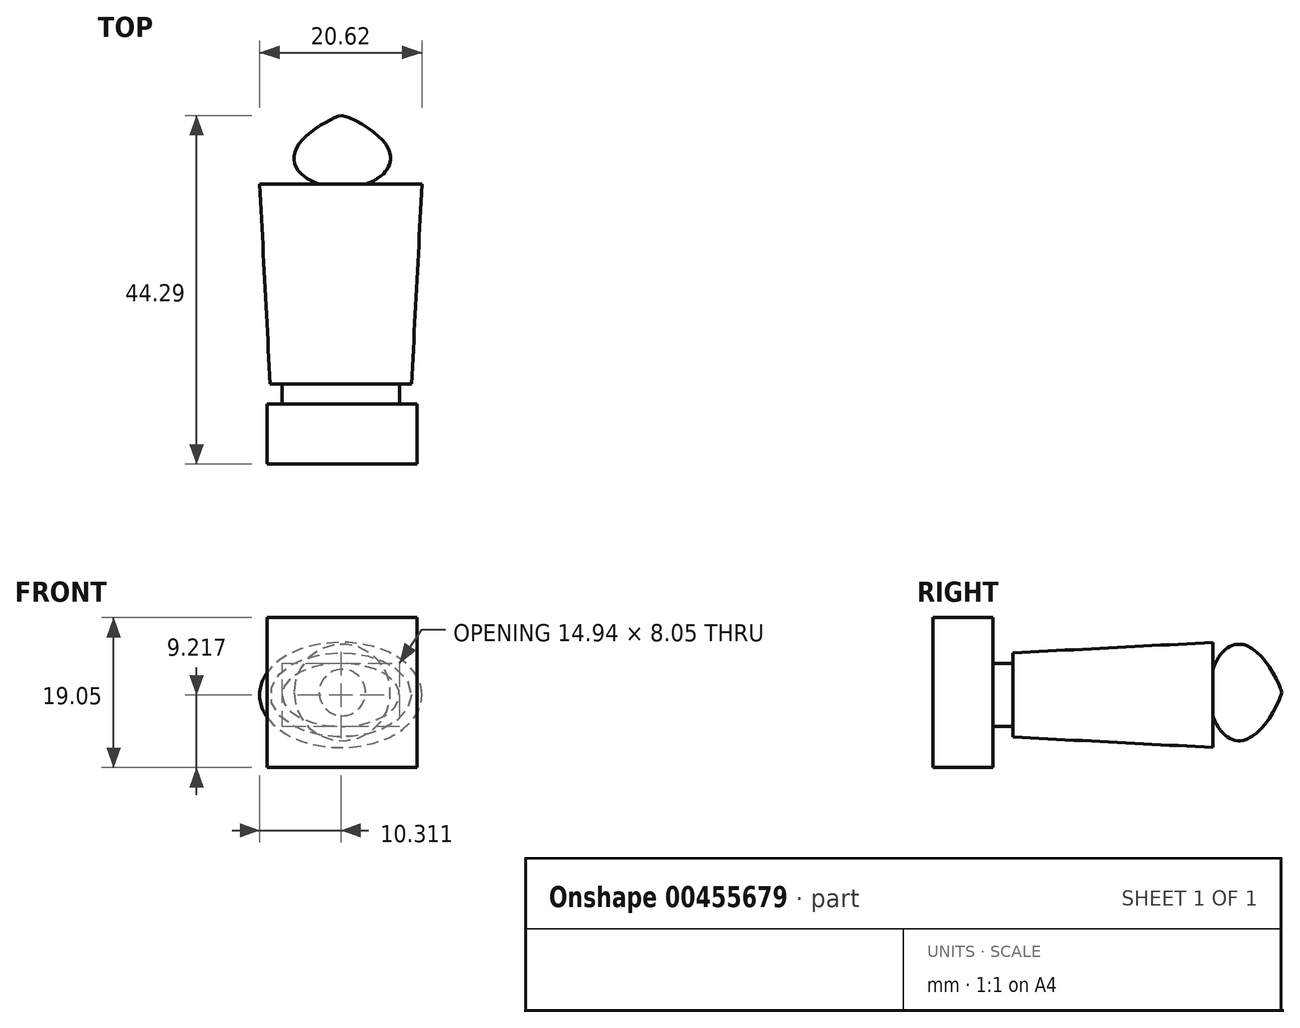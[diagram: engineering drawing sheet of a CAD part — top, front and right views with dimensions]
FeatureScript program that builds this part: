
annotation { "Feature Type Name" : "Feature", "Feature Type Description" : "" }
export const myFeature = defineFeature(function(context is Context, id is Id, definition is map)
    precondition{}
    {
        {
            var Q0;
            Q0=qCreatedBy(makeId("Front.planeOp"),FACE);
            var sketch = newSketch(context, id + "F0", { "sketchPlane" : qUnion([Q0])});
            skLineSegment(sketch, "E0.bottom", {"start": v(0, 0) * mm, "end": v(-19.05, 0) * mm});
            skLineSegment(sketch, "E0.top", {"start": v(0, 19.05) * mm, "end": v(-19.05, 19.05) * mm});
            skLineSegment(sketch, "E0.left", {"start": v(0, 0) * mm, "end": v(0, 19.05) * mm});
            skLineSegment(sketch, "E0.right", {"start": v(-19.05, 0) * mm, "end": v(-19.05, 19.05) * mm});
            skPoint(sketch, "E1", {"position": v(-9.53, 9.52) * mm});
            skPoint(sketch, "E1.positionSnap0", {"position": v(-19.05, 9.52) * mm});
            skPoint(sketch, "E1.positionSnap1", {"position": v(-9.53, 19.05) * mm});
            skSolve(sketch);
        }
        {
            var Q0;
            Q0=makeQuery(id+"F0.imprint","IMPRINT",FACE,{"disambiguationData":[TD([[makeQuery(id+"F0.imprint","IMPRINT",EDGE,{"derivedFrom":sQuery(id+"F0.wireOp",EDGE,"E0.bottom")}),-1.0]])]});
            extrude(context, id + "F1", {"entities" : qUnion([Q0]), "depth" : 7.62 * mm});
        }
        {
            var Q0;
            Q0=qCreatedBy(makeId("Front.planeOp"),FACE);
            var sketch = newSketch(context, id + "F2", { "sketchPlane" : qUnion([Q0])});
            skPoint(sketch, "E2", {"position": v(-9.7, 9.22) * mm});
            skEllipse(sketch, "E3", {"center": v(-9.7, 9.22) * mm, "majorRadius": 7.47 * mm, "minorRadius": 4.02 * mm, "majorAxis": v(-1, 0)});
            skSolve(sketch);
        }
        {
            var Q0;
            Q0=makeQuery(id+"F2.imprint","IMPRINT",FACE,{"disambiguationData":[TD([[makeQuery(id+"F2.imprint","IMPRINT",EDGE,{"derivedFrom":sQuery(id+"F2.wireOp",EDGE,"E3")}),1.0]])]});
            extrude(context, id + "F3", {"entities" : qUnion([Q0]), "operationType" : NewBodyOperationType.ADD, "oppositeDirection" : true, "depth" : 2.54 * mm});
        }
        {
            var Q0;
            Q0=makeQuery(id+"F3.opExtrude","CAP_FACE",FACE,{"disambiguationData":[OSD([sQuery(id+"F2.wireOp",EDGE,"E3")])],"isStart":false});
            var sketch = newSketch(context, id + "F4", { "sketchPlane" : qUnion([Q0])});
            skEllipse(sketch, "E4", {"center": v(9.7, 9.22) * mm, "majorRadius": 8.98 * mm, "minorRadius": 5.34 * mm, "majorAxis": v(1, 0)});
            skSolve(sketch);
        }
        {
            var Q0;
            Q0=makeQuery(id+"F4.imprint","IMPRINT",FACE,{"disambiguationData":[TD([[makeQuery(id+"F4.imprint","IMPRINT",EDGE,{"derivedFrom":sQuery(id+"F4.wireOp",EDGE,"E4")}),1.0]])]});
            var Q1;
            Q1=makeQuery(id+"F4.imprint","IMPRINT",FACE,{"disambiguationData":[TD([[makeQuery(id+"F4.imprint","IMPRINT",EDGE,{"derivedFrom":makeQuery(id+"F3.opExtrude","CAP_EDGE",EDGE,{"disambiguationData":[OSD([sQuery(id+"F2.wireOp",EDGE,"E3")])],"isStart":false})}),-1.0]])]});
            extrude(context, id + "F5", {"entities" : qUnion([Q0, Q1]), "operationType" : NewBodyOperationType.ADD, "depth" : 25.4 * mm, "hasDraft" : true, "draftAngle" : 3 * degree});
        }
        {
            var Q0;
            Q0=makeQuery(id+"F1.opExtrude","SWEPT_FACE",FACE,{"disambiguationData":[OSD([sQuery(id+"F0.wireOp",EDGE,"E0.bottom")])]});
            var Q1;
            Q1=makeQuery(id+"F1.opExtrude","SWEPT_FACE",FACE,{"disambiguationData":[OSD([sQuery(id+"F0.wireOp",EDGE,"E0.top")])]});
            cPlane(context, id + "F6", {"entities" : qUnion([Q0, Q1]), "cplaneType" : CPlaneType.MID_PLANE, "offset" : 25.4 * mm, "width" : 152.4 * mm, "height" : 152.4 * mm});
        }
        {
            var Q0;
            Q0=qCreatedBy(id+"F6.planeOp",FACE);
            var sketch = newSketch(context, id + "F7", { "sketchPlane" : qUnion([Q0])});
            skLineSegment(sketch, "E5", {"start": v(-9.53, -33.07) * mm, "end": v(-9.53, 18.26) * mm, "construction": true});
            skLineSegment(sketch, "E6", {"start": v(-9.53, -36.67) * mm, "end": v(-9.53, -27.02) * mm});
            skFitSpline(sketch, "E7", {"points": [v(-9.53, -36.67) * mm, v(-15.42, -32.37) * mm, v(-14.19, -28.77) * mm, v(-9.53, -27.02) * mm], "startDerivative": vector(-11.78, 2.18) * mm, "endDerivative": vector(11.97, 4.73) * mm});
            skSolve(sketch);
        }
        {
            var Q0;
            Q0=makeQuery(id+"F7.imprint","IMPRINT",FACE,{"disambiguationData":[TD([[makeQuery(id+"F7.imprint","IMPRINT",EDGE,{"derivedFrom":sQuery(id+"F7.wireOp",EDGE,"E6")}),1.0]])]});
            var Q1;
            Q1=sQuery(id+"F7.wireOp",EDGE,"E6");
            revolve(context, id + "F8", {"operationType" : NewBodyOperationType.ADD, "entities" : qUnion([Q0]), "axis" : qUnion([Q1]), "revolveType" : RevolveType.FULL});
        }
    });
